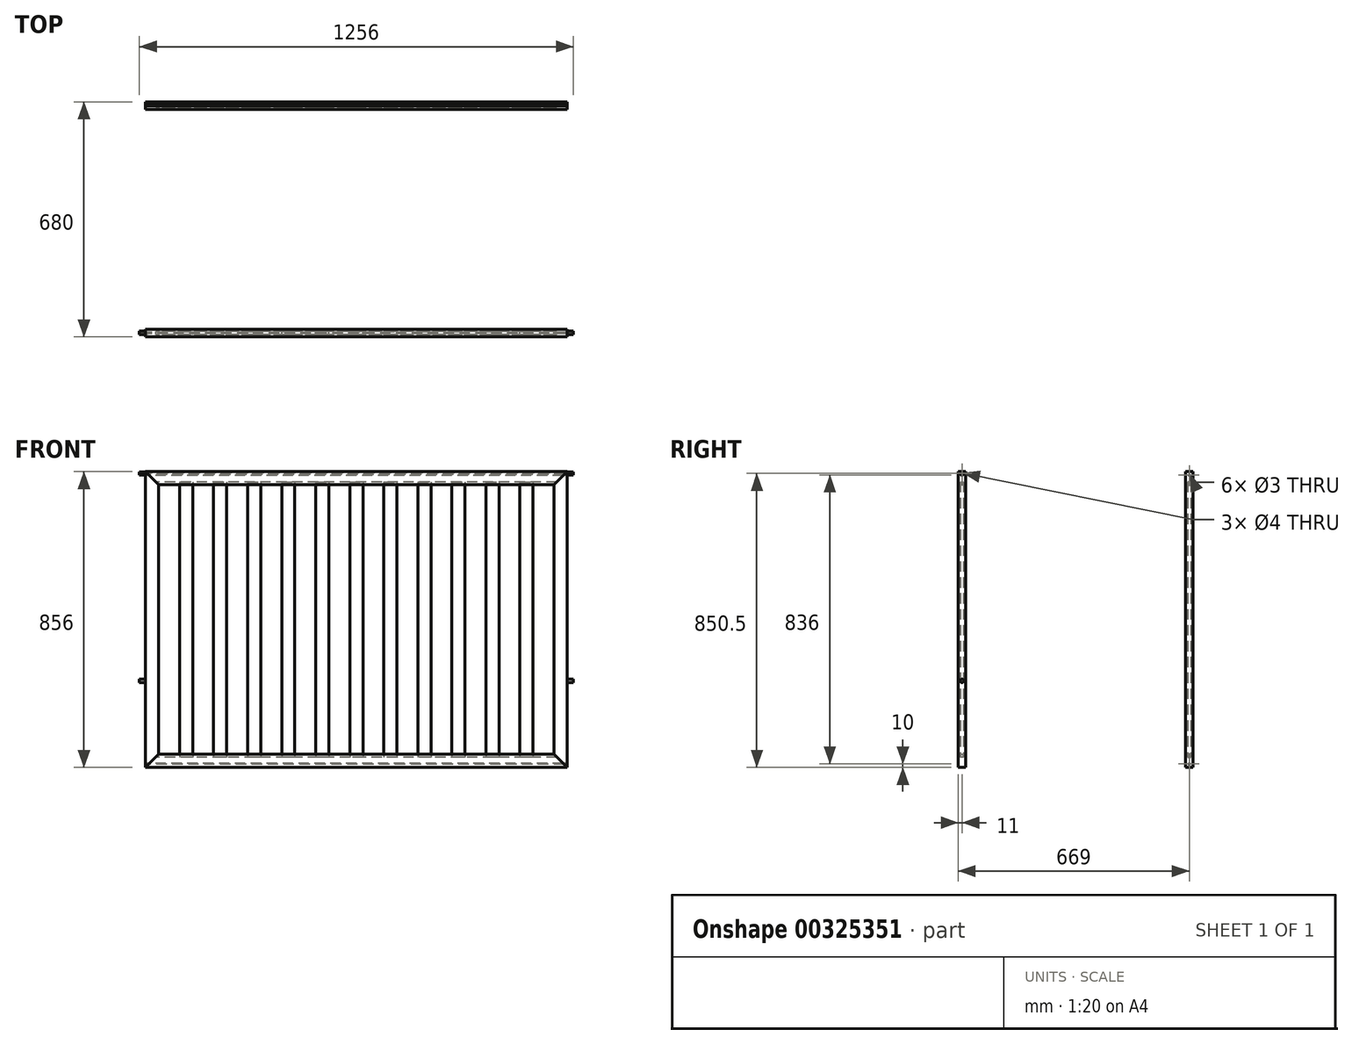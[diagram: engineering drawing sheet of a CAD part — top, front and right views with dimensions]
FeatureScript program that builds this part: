
annotation { "Feature Type Name" : "Feature", "Feature Type Description" : "" }
export const myFeature = defineFeature(function(context is Context, id is Id, definition is map)
    precondition{}
    {
        {
            var Q0;
            Q0=qCreatedBy(makeId("Right.planeOp"),FACE);
            var sketch = newSketch(context, id + "F0", { "sketchPlane" : qUnion([Q0])});
            skLineSegment(sketch, "E0", {"start": v(0, 0) * mm, "end": v(340, 0) * mm, "construction": true});
            skLineSegment(sketch, "E1", {"start": v(340, 0) * mm, "end": v(340, 428) * mm, "construction": true});
            skLineSegment(sketch, "E2.bottom", {"start": v(318, 428) * mm, "end": v(340, 428) * mm});
            skLineSegment(sketch, "E2.top", {"start": v(318, 390) * mm, "end": v(324.5, 390) * mm});
            skLineSegment(sketch, "E2.left", {"start": v(318, 428) * mm, "end": v(318, 390) * mm});
            skLineSegment(sketch, "E2.right", {"start": v(340, 428) * mm, "end": v(340, 390) * mm});
            skLineSegment(sketch, "E3.bottom", {"start": v(333.5, 398) * mm, "end": v(324.5, 398) * mm});
            skLineSegment(sketch, "E3.left", {"start": v(333.5, 398) * mm, "end": v(333.5, 390) * mm});
            skLineSegment(sketch, "E3.right", {"start": v(324.5, 398) * mm, "end": v(324.5, 390) * mm});
            skPoint(sketch, "E3.middle", {"position": v(329, 390) * mm});
            skLineSegment(sketch, "E4.trimOffspring", {"start": v(333.5, 390) * mm, "end": v(340, 390) * mm});
            skLineSegment(sketch, "E5.MirrorCS", {"start": v(318, -390) * mm, "end": v(324.5, -390) * mm});
            skLineSegment(sketch, "E6.MirrorCS", {"start": v(333.5, -390) * mm, "end": v(340, -390) * mm});
            skPoint(sketch, "E7.MirrorP", {"position": v(329, -390) * mm});
            skLineSegment(sketch, "E8.MirrorCS", {"start": v(333.5, -398) * mm, "end": v(333.5, -390) * mm});
            skLineSegment(sketch, "E9.MirrorCS", {"start": v(324.5, -398) * mm, "end": v(324.5, -390) * mm});
            skLineSegment(sketch, "E10.MirrorCS", {"start": v(318, -428) * mm, "end": v(340, -428) * mm});
            skLineSegment(sketch, "E11.MirrorCS", {"start": v(318, -428) * mm, "end": v(318, -390) * mm});
            skLineSegment(sketch, "E12.MirrorCS", {"start": v(333.5, -398) * mm, "end": v(324.5, -398) * mm});
            skLineSegment(sketch, "E13.MirrorCS", {"start": v(340, -428) * mm, "end": v(340, -390) * mm});
            skSolve(sketch);
        }
        {
            var Q0;
            Q0 = qSketchRegion(id + "F0", true);
            extrude(context, id + "F1", {"entities" : qUnion([Q0]), "depth" : 1220 * mm});
        }
        {
            var Q0;
            Q0=makeQuery(id+"F1.opExtrude","SWEPT_FACE",FACE,{"disambiguationData":[OSD([sQuery(id+"F0.wireOp",EDGE,"E2.left")])]});
            var sketch = newSketch(context, id + "F2", { "sketchPlane" : qUnion([Q0])});
            skPoint(sketch, "E14.0", {"position": v(0, 428) * mm});
            skLineSegment(sketch, "E15", {"start": v(0, 0) * mm, "end": v(-300, 0) * mm, "construction": true});
            skPoint(sketch, "E16.MirrorP", {"position": v(0, -428) * mm});
            skLineSegment(sketch, "E17", {"start": v(0, -428) * mm, "end": v(0, 428) * mm});
            skLineSegment(sketch, "E18", {"start": v(38, 390) * mm, "end": v(38, -390) * mm});
            skPoint(sketch, "E19.0", {"position": v(610, 428) * mm});
            skLineSegment(sketch, "E20", {"start": v(610, 428) * mm, "end": v(610, 568) * mm, "construction": true});
            skLineSegment(sketch, "E21", {"start": v(38, 390) * mm, "end": v(0, 428) * mm});
            skLineSegment(sketch, "E22", {"start": v(0, -428) * mm, "end": v(38, -390) * mm});
            skPoint(sketch, "E23.orphan", {"position": v(0, -390) * mm});
            skLineSegment(sketch, "E24.MirrorCS", {"start": v(1182, 390) * mm, "end": v(1220, 428) * mm});
            skLineSegment(sketch, "E25.MirrorCS", {"start": v(1220, -428) * mm, "end": v(1182, -390) * mm});
            skPoint(sketch, "E26.MirrorP", {"position": v(1220, -390) * mm});
            skPoint(sketch, "E27.MirrorP", {"position": v(1220, 428) * mm});
            skLineSegment(sketch, "E28.MirrorCS", {"start": v(1182, 390) * mm, "end": v(1182, -390) * mm});
            skLineSegment(sketch, "E29.MirrorCS", {"start": v(1220, -428) * mm, "end": v(1220, 428) * mm});
            skPoint(sketch, "E30.MirrorP", {"position": v(1220, -428) * mm});
            skSolve(sketch);
        }
        {
            var Q0;
            Q0 = qSketchRegion(id + "F2", true);
            extrude(context, id + "F3", {"entities" : qUnion([Q0]), "operationType" : NewBodyOperationType.REMOVE, "oppositeDirection" : true, "depth" : 350 * mm});
        }
        {
            var Q0;
            Q0 = qSketchRegion(id + "F2", true);
            extrude(context, id + "F4", {"entities" : qUnion([Q0]), "oppositeDirection" : true, "depth" : 22 * mm});
        }
        {
            var Q0;
            Q0=makeQuery(id+"F1.opExtrude","SWEPT_FACE",FACE,{"disambiguationData":[OSD([sQuery(id+"F0.wireOp",EDGE,"E12.MirrorCS")])]});
            var sketch = newSketch(context, id + "F5", { "sketchPlane" : qUnion([Q0])});
            skLineSegment(sketch, "E31.0", {"start": v(98.5, 324.5) * mm, "end": v(38, 324.5) * mm, "construction": true});
            skPoint(sketch, "E32.orphan", {"position": v(38, 324.5) * mm});
            skLineSegment(sketch, "E33.bottom", {"start": v(98.5, 324.5) * mm, "end": v(136.5, 324.5) * mm});
            skLineSegment(sketch, "E33.top", {"start": v(98.5, 333.5) * mm, "end": v(136.5, 333.5) * mm});
            skLineSegment(sketch, "E33.left", {"start": v(98.5, 324.5) * mm, "end": v(98.5, 333.5) * mm});
            skLineSegment(sketch, "E33.right", {"start": v(136.5, 324.5) * mm, "end": v(136.5, 333.5) * mm});
            skLineSegment(sketch, "E34.1.0.0", {"start": v(197, 333.5) * mm, "end": v(235, 333.5) * mm});
            skLineSegment(sketch, "E34.1.0.1", {"start": v(197, 324.5) * mm, "end": v(197, 333.5) * mm});
            skLineSegment(sketch, "E34.1.0.2", {"start": v(197, 324.5) * mm, "end": v(235, 324.5) * mm});
            skLineSegment(sketch, "E34.1.0.3", {"start": v(235, 324.5) * mm, "end": v(235, 333.5) * mm});
            skLineSegment(sketch, "E34.2.0.0", {"start": v(295.5, 333.5) * mm, "end": v(333.5, 333.5) * mm});
            skLineSegment(sketch, "E34.2.0.1", {"start": v(295.5, 324.5) * mm, "end": v(295.5, 333.5) * mm});
            skLineSegment(sketch, "E34.2.0.2", {"start": v(295.5, 324.5) * mm, "end": v(333.5, 324.5) * mm});
            skLineSegment(sketch, "E34.2.0.3", {"start": v(333.5, 324.5) * mm, "end": v(333.5, 333.5) * mm});
            skLineSegment(sketch, "E34.3.0.0", {"start": v(394, 333.5) * mm, "end": v(432, 333.5) * mm});
            skLineSegment(sketch, "E34.3.0.1", {"start": v(394, 324.5) * mm, "end": v(394, 333.5) * mm});
            skLineSegment(sketch, "E34.3.0.2", {"start": v(394, 324.5) * mm, "end": v(432, 324.5) * mm});
            skLineSegment(sketch, "E34.3.0.3", {"start": v(432, 324.5) * mm, "end": v(432, 333.5) * mm});
            skLineSegment(sketch, "E34.4.0.0", {"start": v(492.5, 333.5) * mm, "end": v(530.5, 333.5) * mm});
            skLineSegment(sketch, "E34.4.0.1", {"start": v(492.5, 324.5) * mm, "end": v(492.5, 333.5) * mm});
            skLineSegment(sketch, "E34.4.0.2", {"start": v(492.5, 324.5) * mm, "end": v(530.5, 324.5) * mm});
            skLineSegment(sketch, "E34.4.0.3", {"start": v(530.5, 324.5) * mm, "end": v(530.5, 333.5) * mm});
            skLineSegment(sketch, "E34.5.0.0", {"start": v(591, 333.5) * mm, "end": v(629, 333.5) * mm});
            skLineSegment(sketch, "E34.5.0.1", {"start": v(591, 324.5) * mm, "end": v(591, 333.5) * mm});
            skLineSegment(sketch, "E34.5.0.2", {"start": v(591, 324.5) * mm, "end": v(629, 324.5) * mm});
            skLineSegment(sketch, "E34.5.0.3", {"start": v(629, 324.5) * mm, "end": v(629, 333.5) * mm});
            skLineSegment(sketch, "E34.6.0.0", {"start": v(689.5, 333.5) * mm, "end": v(727.5, 333.5) * mm});
            skLineSegment(sketch, "E34.6.0.1", {"start": v(689.5, 324.5) * mm, "end": v(689.5, 333.5) * mm});
            skLineSegment(sketch, "E34.6.0.2", {"start": v(689.5, 324.5) * mm, "end": v(727.5, 324.5) * mm});
            skLineSegment(sketch, "E34.6.0.3", {"start": v(727.5, 324.5) * mm, "end": v(727.5, 333.5) * mm});
            skLineSegment(sketch, "E34.7.0.0", {"start": v(788, 333.5) * mm, "end": v(826, 333.5) * mm});
            skLineSegment(sketch, "E34.7.0.1", {"start": v(788, 324.5) * mm, "end": v(788, 333.5) * mm});
            skLineSegment(sketch, "E34.7.0.2", {"start": v(788, 324.5) * mm, "end": v(826, 324.5) * mm});
            skLineSegment(sketch, "E34.7.0.3", {"start": v(826, 324.5) * mm, "end": v(826, 333.5) * mm});
            skLineSegment(sketch, "E34.8.0.0", {"start": v(886.5, 333.5) * mm, "end": v(924.5, 333.5) * mm});
            skLineSegment(sketch, "E34.8.0.1", {"start": v(886.5, 324.5) * mm, "end": v(886.5, 333.5) * mm});
            skLineSegment(sketch, "E34.8.0.2", {"start": v(886.5, 324.5) * mm, "end": v(924.5, 324.5) * mm});
            skLineSegment(sketch, "E34.8.0.3", {"start": v(924.5, 324.5) * mm, "end": v(924.5, 333.5) * mm});
            skLineSegment(sketch, "E34.9.0.0", {"start": v(985, 333.5) * mm, "end": v(1023, 333.5) * mm});
            skLineSegment(sketch, "E34.9.0.1", {"start": v(985, 324.5) * mm, "end": v(985, 333.5) * mm});
            skLineSegment(sketch, "E34.9.0.2", {"start": v(985, 324.5) * mm, "end": v(1023, 324.5) * mm});
            skLineSegment(sketch, "E34.9.0.3", {"start": v(1023, 324.5) * mm, "end": v(1023, 333.5) * mm});
            skLineSegment(sketch, "E34.10.0.0", {"start": v(1083.5, 333.5) * mm, "end": v(1121.5, 333.5) * mm});
            skLineSegment(sketch, "E34.10.0.1", {"start": v(1083.5, 324.5) * mm, "end": v(1083.5, 333.5) * mm});
            skLineSegment(sketch, "E34.10.0.2", {"start": v(1083.5, 324.5) * mm, "end": v(1121.5, 324.5) * mm});
            skLineSegment(sketch, "E34.10.0.3", {"start": v(1121.5, 324.5) * mm, "end": v(1121.5, 333.5) * mm});
            skLineSegment(sketch, "E34.direction1", {"start": v(98.5, 324.5) * mm, "end": v(197, 324.5) * mm, "construction": true});
            skSolve(sketch);
        }
        {
            var Q0;
            Q0 = qSketchRegion(id + "F5", true);
            var Q1;
            Q1=makeQuery(id+"F1.opExtrude","SWEPT_FACE",FACE,{"disambiguationData":[OSD([sQuery(id+"F0.wireOp",EDGE,"E3.bottom")])]});
            extrude(context, id + "F6", {"entities" : qUnion([Q0]), "endBound" : BoundingType.UP_TO_SURFACE, "endBoundEntityFace" : qUnion([Q1]), "depth" : 25 * mm});
        }
        {
            var Q0;
            Q0=qCreatedBy(makeId("Right.planeOp"),FACE);
            var sketch = newSketch(context, id + "F7", { "sketchPlane" : qUnion([Q0])});
            skLineSegment(sketch, "E35.bottom", {"start": v(318, 435) * mm, "end": v(340, 435) * mm, "construction": true});
            skLineSegment(sketch, "E35.top", {"start": v(318, 400) * mm, "end": v(340, 400) * mm, "construction": true});
            skLineSegment(sketch, "E35.left", {"start": v(318, 435) * mm, "end": v(318, 400) * mm, "construction": true});
            skLineSegment(sketch, "E35.right", {"start": v(340, 435) * mm, "end": v(340, 400) * mm, "construction": true});
            skLineSegment(sketch, "E36", {"start": v(329, 435) * mm, "end": v(329, 429) * mm, "construction": true});
            skLineSegment(sketch, "E37", {"start": v(329, 429) * mm, "end": v(329, 418) * mm, "construction": true});
            skCircle(sketch, "E38", {"center": v(329, 429) * mm, "radius": 2.5 * mm});
            skCircle(sketch, "E39", {"center": v(329, 418) * mm, "radius": 2.5 * mm});
            skLineSegment(sketch, "E40", {"start": v(0, 0) * mm, "end": v(-140, 0) * mm, "construction": true});
            skLineSegment(sketch, "E41.MirrorCS", {"start": v(318, -435) * mm, "end": v(340, -435) * mm, "construction": true});
            skLineSegment(sketch, "E42.MirrorCS", {"start": v(340, -435) * mm, "end": v(340, -400) * mm, "construction": true});
            skLineSegment(sketch, "E43.MirrorCS", {"start": v(318, -435) * mm, "end": v(318, -400) * mm, "construction": true});
            skLineSegment(sketch, "E44.MirrorCS", {"start": v(318, -400) * mm, "end": v(340, -400) * mm, "construction": true});
            skCircle(sketch, "E45.MirrorC", {"center": v(329, -418) * mm, "radius": 2.5 * mm});
            skCircle(sketch, "E46.MirrorC", {"center": v(329, -429) * mm, "radius": 2.5 * mm});
            skLineSegment(sketch, "E47", {"start": v(0, 0) * mm, "end": v(0, 200) * mm, "construction": true});
            skLineSegment(sketch, "E48.MirrorCS", {"start": v(-318, -435) * mm, "end": v(-318, -400) * mm, "construction": true});
            skLineSegment(sketch, "E49.MirrorCS", {"start": v(-318, -400) * mm, "end": v(-340, -400) * mm, "construction": true});
            skLineSegment(sketch, "E50.MirrorCS", {"start": v(-340, -435) * mm, "end": v(-340, -400) * mm, "construction": true});
            skLineSegment(sketch, "E51.MirrorCS", {"start": v(-318, -435) * mm, "end": v(-340, -435) * mm, "construction": true});
            skLineSegment(sketch, "E52.MirrorCS", {"start": v(-318, 400) * mm, "end": v(-340, 400) * mm, "construction": true});
            skLineSegment(sketch, "E53.MirrorCS", {"start": v(-318, 435) * mm, "end": v(-318, 400) * mm, "construction": true});
            skLineSegment(sketch, "E54.MirrorCS", {"start": v(-340, 435) * mm, "end": v(-340, 400) * mm, "construction": true});
            skLineSegment(sketch, "E55.MirrorCS", {"start": v(-318, 435) * mm, "end": v(-340, 435) * mm, "construction": true});
            skLineSegment(sketch, "E56", {"start": v(-329, 435) * mm, "end": v(-329, 422.5) * mm, "construction": true});
            skPoint(sketch, "E56.endSnap0", {"position": v(-329, 435) * mm});
            skArc(sketch, "E57", {"start": v(-323.5, 422.5) * mm, "mid": v(-329, 428) * mm, "end": v(-334.5, 422.5) * mm});
            skArc(sketch, "E58.0.1.0", {"start": v(-334.5, 282.5) * mm, "mid": v(-329, 277) * mm, "end": v(-323.5, 282.5) * mm});
            skLineSegment(sketch, "E58.direction2", {"start": v(-329, 422.5) * mm, "end": v(-329, 282.5) * mm, "construction": true});
            skLineSegment(sketch, "E59.0", {"start": v(-334.5, 422.5) * mm, "end": v(-334.5, 282.5) * mm});
            skLineSegment(sketch, "E60.0.1.0", {"start": v(-334.5, -177.5) * mm, "end": v(-334.5, -317.5) * mm});
            skArc(sketch, "E60.0.1.2", {"start": v(-323.5, -177.5) * mm, "mid": v(-329, -172) * mm, "end": v(-334.5, -177.5) * mm});
            skArc(sketch, "E60.0.1.3", {"start": v(-334.5, -317.5) * mm, "mid": v(-329, -323) * mm, "end": v(-323.5, -317.5) * mm});
            skLineSegment(sketch, "E60.direction1", {"start": v(-334.5, 282.5) * mm, "end": v(-313.5, 282.5) * mm, "construction": true});
            skLineSegment(sketch, "E60.direction2", {"start": v(-334.5, 282.5) * mm, "end": v(-334.5, -317.5) * mm, "construction": true});
            skLineSegment(sketch, "E61", {"start": v(-323.5, -317.5) * mm, "end": v(-323.5, -177.5) * mm});
            skSolve(sketch);
        }
        {
            var Q0;
            Q0=makeQuery(id+"F4.opExtrude","SWEPT_BODY",BODY,{"disambiguationData":[OSD([sQuery(id+"F2.wireOp",EDGE,"b1047d30-6eb7-4597-bc75-de0ae35a6d8d0.MirrorCS"),sQuery(id+"F2.wireOp",EDGE,"b1047d30-6eb7-4597-bc75-de0ae35a6d8d1.MirrorCS"),sQuery(id+"F2.wireOp",EDGE,"b1047d30-6eb7-4597-bc75-de0ae35a6d8d3.MirrorCS"),sQuery(id+"F2.wireOp",EDGE,"b1047d30-6eb7-4597-bc75-de0ae35a6d8d4.MirrorCS")])]});
            var Q1;
            Q1=makeQuery(id+"F6.opExtrude","SWEPT_BODY",BODY,{"disambiguationData":[OSD([sQuery(id+"F5.wireOp",EDGE,"E34.6.0.0"),sQuery(id+"F5.wireOp",EDGE,"E34.6.0.1"),sQuery(id+"F5.wireOp",EDGE,"E34.6.0.2"),sQuery(id+"F5.wireOp",EDGE,"E34.6.0.3")])]});
            var Q2;
            Q2=makeQuery(id+"F6.opExtrude","SWEPT_BODY",BODY,{"disambiguationData":[OSD([sQuery(id+"F5.wireOp",EDGE,"E34.11.0.0"),sQuery(id+"F5.wireOp",EDGE,"E34.11.0.1"),sQuery(id+"F5.wireOp",EDGE,"E34.11.0.2"),sQuery(id+"F5.wireOp",EDGE,"E34.11.0.3")])]});
            var Q3;
            Q3=makeQuery(id+"F6.opExtrude","SWEPT_BODY",BODY,{"disambiguationData":[OSD([sQuery(id+"F5.wireOp",EDGE,"E34.5.0.0"),sQuery(id+"F5.wireOp",EDGE,"E34.5.0.1"),sQuery(id+"F5.wireOp",EDGE,"E34.5.0.2"),sQuery(id+"F5.wireOp",EDGE,"E34.5.0.3")])]});
            var Q4;
            Q4=makeQuery(id+"F6.opExtrude","SWEPT_BODY",BODY,{"disambiguationData":[OSD([sQuery(id+"F5.wireOp",EDGE,"E34.7.0.0"),sQuery(id+"F5.wireOp",EDGE,"E34.7.0.1"),sQuery(id+"F5.wireOp",EDGE,"E34.7.0.2"),sQuery(id+"F5.wireOp",EDGE,"E34.7.0.3")])]});
            var Q5;
            Q5=makeQuery(id+"F6.opExtrude","SWEPT_BODY",BODY,{"disambiguationData":[OSD([sQuery(id+"F5.wireOp",EDGE,"E34.10.0.0"),sQuery(id+"F5.wireOp",EDGE,"E34.10.0.1"),sQuery(id+"F5.wireOp",EDGE,"E34.10.0.2"),sQuery(id+"F5.wireOp",EDGE,"E34.10.0.3")])]});
            var Q6;
            Q6=makeQuery(id+"F6.opExtrude","SWEPT_BODY",BODY,{"disambiguationData":[OSD([sQuery(id+"F5.wireOp",EDGE,"E34.4.0.0"),sQuery(id+"F5.wireOp",EDGE,"E34.4.0.1"),sQuery(id+"F5.wireOp",EDGE,"E34.4.0.2"),sQuery(id+"F5.wireOp",EDGE,"E34.4.0.3")])]});
            var Q7;
            Q7=makeQuery(id+"F6.opExtrude","SWEPT_BODY",BODY,{"disambiguationData":[OSD([sQuery(id+"F5.wireOp",EDGE,"E34.9.0.0"),sQuery(id+"F5.wireOp",EDGE,"E34.9.0.1"),sQuery(id+"F5.wireOp",EDGE,"E34.9.0.2"),sQuery(id+"F5.wireOp",EDGE,"E34.9.0.3")])]});
            var Q8;
            Q8=makeQuery(id+"F6.opExtrude","SWEPT_BODY",BODY,{"disambiguationData":[OSD([sQuery(id+"F5.wireOp",EDGE,"E34.3.0.0"),sQuery(id+"F5.wireOp",EDGE,"E34.3.0.1"),sQuery(id+"F5.wireOp",EDGE,"E34.3.0.2"),sQuery(id+"F5.wireOp",EDGE,"E34.3.0.3")])]});
            var Q9;
            Q9=makeQuery(id+"F6.opExtrude","SWEPT_BODY",BODY,{"disambiguationData":[OSD([sQuery(id+"F5.wireOp",EDGE,"E34.2.0.0"),sQuery(id+"F5.wireOp",EDGE,"E34.2.0.1"),sQuery(id+"F5.wireOp",EDGE,"E34.2.0.2"),sQuery(id+"F5.wireOp",EDGE,"E34.2.0.3")])]});
            var Q10;
            Q10=makeQuery(id+"F6.opExtrude","SWEPT_BODY",BODY,{"disambiguationData":[OSD([sQuery(id+"F5.wireOp",EDGE,"E33.bottom"),sQuery(id+"F5.wireOp",EDGE,"E33.top"),sQuery(id+"F5.wireOp",EDGE,"E33.left"),sQuery(id+"F5.wireOp",EDGE,"E33.right")])]});
            var Q11;
            Q11=makeQuery(id+"F6.opExtrude","SWEPT_BODY",BODY,{"disambiguationData":[OSD([sQuery(id+"F5.wireOp",EDGE,"E34.1.0.0"),sQuery(id+"F5.wireOp",EDGE,"E34.1.0.1"),sQuery(id+"F5.wireOp",EDGE,"E34.1.0.2"),sQuery(id+"F5.wireOp",EDGE,"E34.1.0.3")])]});
            var Q12;
            Q12=makeQuery(id+"F1.opExtrude","SWEPT_BODY",BODY,{"disambiguationData":[OSD([sQuery(id+"F0.wireOp",EDGE,"E2.bottom"),sQuery(id+"F0.wireOp",EDGE,"E2.top"),sQuery(id+"F0.wireOp",EDGE,"E2.left"),sQuery(id+"F0.wireOp",EDGE,"E2.right"),sQuery(id+"F0.wireOp",EDGE,"E3.bottom"),sQuery(id+"F0.wireOp",EDGE,"E3.left"),sQuery(id+"F0.wireOp",EDGE,"E3.right"),sQuery(id+"F0.wireOp",EDGE,"E4.trimOffspring")])]});
            var Q13;
            Q13=makeQuery(id+"F6.opExtrude","SWEPT_BODY",BODY,{"disambiguationData":[OSD([sQuery(id+"F5.wireOp",EDGE,"E34.8.0.0"),sQuery(id+"F5.wireOp",EDGE,"E34.8.0.1"),sQuery(id+"F5.wireOp",EDGE,"E34.8.0.2"),sQuery(id+"F5.wireOp",EDGE,"E34.8.0.3")])]});
            var Q14;
            Q14=makeQuery(id+"F4.opExtrude","SWEPT_BODY",BODY,{"disambiguationData":[OSD([sQuery(id+"F2.wireOp",EDGE,"6JQJvKk6-9tsE-XuLx-Z2kx-k19th0KeuHWZ"),sQuery(id+"F2.wireOp",EDGE,"8ad1f134-3218-4958-96c1-cced4667ce510.MirrorCS"),sQuery(id+"F2.wireOp",EDGE,"E17"),sQuery(id+"F2.wireOp",EDGE,"E18")])]});
            var Q15;
            Q15=makeQuery(id+"F1.opExtrude","SWEPT_BODY",BODY,{"disambiguationData":[OSD([sQuery(id+"F0.wireOp",EDGE,"E5.MirrorCS"),sQuery(id+"F0.wireOp",EDGE,"E6.MirrorCS"),sQuery(id+"F0.wireOp",EDGE,"E8.MirrorCS"),sQuery(id+"F0.wireOp",EDGE,"E9.MirrorCS"),sQuery(id+"F0.wireOp",EDGE,"E10.MirrorCS"),sQuery(id+"F0.wireOp",EDGE,"E11.MirrorCS"),sQuery(id+"F0.wireOp",EDGE,"E12.MirrorCS"),sQuery(id+"F0.wireOp",EDGE,"E13.MirrorCS")])]});
            var Q16;
            Q16=makeQuery(id+"F4.opExtrude","SWEPT_BODY",BODY,{"disambiguationData":[OSD([sQuery(id+"F2.wireOp",EDGE,"E24.MirrorCS"),sQuery(id+"F2.wireOp",EDGE,"E25.MirrorCS"),sQuery(id+"F2.wireOp",EDGE,"E28.MirrorCS"),sQuery(id+"F2.wireOp",EDGE,"E29.MirrorCS")])]});
            var Q17;
            Q17=qCreatedBy(makeId("Front.planeOp"),FACE);
            mirror(context, id + "F8", {"entities" : qUnion([Q0, Q1, Q2, Q3, Q4, Q5, Q6, Q7, Q8, Q9, Q10, Q11, Q12, Q13, Q14, Q15, Q16]), "mirrorPlane" : qUnion([Q17])});
        }
        {
            var Q0;
            Q0=makeQuery(id+"F4.opExtrude","SWEPT_FACE",FACE,{"disambiguationData":[OSD([sQuery(id+"F2.wireOp",EDGE,"E17")])]});
            var sketch = newSketch(context, id + "F9", { "sketchPlane" : qUnion([Q0])});
            skPoint(sketch, "E62.0", {"position": v(-329, -418) * mm});
            skPoint(sketch, "E62.1", {"position": v(-329, -429) * mm});
            skPoint(sketch, "E62.2", {"position": v(-329, 429) * mm});
            skPoint(sketch, "E62.3", {"position": v(-329, 418) * mm});
            skCircle(sketch, "E63", {"center": v(-329, 429) * mm, "radius": 1.5 * mm});
            skCircle(sketch, "E64", {"center": v(-329, 418) * mm, "radius": 1.5 * mm});
            skCircle(sketch, "E65", {"center": v(-329, -418) * mm, "radius": 1.5 * mm});
            skCircle(sketch, "E66", {"center": v(-329, -429) * mm, "radius": 1.5 * mm});
            skSolve(sketch);
        }
        {
            var Q0;
            Q0 = qSketchRegion(id + "F9", true);
            var Q1;
            Q1 = qConstructionFilter(qBodyType(qCreatedBy(id + "F9" ,EDGE), BodyType.WIRE), ConstructionObject.NO);
            extrude(context, id + "F10", {"entities" : qUnion([Q0]), "operationType" : NewBodyOperationType.REMOVE, "surfaceEntities" : qUnion([Q1]), "endBound" : BoundingType.THROUGH_ALL, "oppositeDirection" : true, "depth" : 50 * mm});
        }
        {
            var Q0;
            Q0=makeQuery(id+"F8.opPattern","COPY",FACE,{"derivedFrom":makeQuery(id+"F4.opExtrude","SWEPT_FACE",FACE,{"disambiguationData":[OSD([sQuery(id+"F2.wireOp",EDGE,"E17")])]}),"instanceName":"1"});
            var sketch = newSketch(context, id + "F11", { "sketchPlane" : qUnion([Q0])});
            skPoint(sketch, "E67.0", {"position": v(329, 422.5) * mm});
            skPoint(sketch, "E68.0", {"position": v(329, -177.5) * mm});
            skCircle(sketch, "E69", {"center": v(329, 422.5) * mm, "radius": 5 * mm});
            skCircle(sketch, "E70", {"center": v(329, -177.5) * mm, "radius": 5 * mm});
            skSolve(sketch);
        }
        {
            var Q0;
            Q0 = qSketchRegion(id + "F11", true);
            extrude(context, id + "F12", {"entities" : qUnion([Q0]), "depth" : 18 * mm});
        }
        {
            var Q0;
            Q0=makeQuery(id+"F8.opPattern","COPY",EDGE,{"derivedFrom":makeQuery(id+"F1.opExtrude","SWEPT_EDGE",EDGE,{"disambiguationData":[OSD([sQuery(id+"F0.wireOp",EDGE,"E2.bottom"),sQuery(id+"F0.wireOp",EDGE,"E2.right")])]}),"instanceName":"1"});
            cPoint(context, id + "F13", {"entities" : qUnion([Q0]), "parameter" : 0.5});
        }
        {
            var Q0;
            Q0=makeQuery(id+"F8.opPattern","COPY",FACE,{"derivedFrom":makeQuery(id+"F4.opExtrude","SWEPT_FACE",FACE,{"disambiguationData":[OSD([sQuery(id+"F2.wireOp",EDGE,"E17")])]}),"instanceName":"1"});
            var Q1;
            Q1 = qCreatedBy(id + "F13" ,VERTEX);
            cPlane(context, id + "F14", {"entities" : qUnion([Q0, Q1]), "cplaneType" : CPlaneType.PLANE_POINT, "offset" : 25 * mm, "width" : 150 * mm, "height" : 150 * mm});
        }
        {
            var Q0;
            Q0=makeQuery(id+"F12.opExtrude","SWEPT_BODY",BODY,{"disambiguationData":[OSD([sQuery(id+"F11.wireOp",EDGE,"E69")])]});
            var Q1;
            Q1=makeQuery(id+"F12.opExtrude","SWEPT_BODY",BODY,{"disambiguationData":[OSD([sQuery(id+"F11.wireOp",EDGE,"E70")])]});
            var Q2;
            Q2=qCreatedBy(id+"F14.planeOp",FACE);
            mirror(context, id + "F15", {"operationType" : NewBodyOperationType.ADD, "entities" : qUnion([Q0, Q1]), "mirrorPlane" : qUnion([Q2])});
        }
        {
            var Q0;
            Q0=makeQuery(id+"F12.opExtrude","CAP_FACE",FACE,{"disambiguationData":[OSD([sQuery(id+"F11.wireOp",EDGE,"E69")])],"isStart":false});
            var sketch = newSketch(context, id + "F16", { "sketchPlane" : qUnion([Q0])});
            skCircle(sketch, "E71", {"center": v(329, 422.5) * mm, "radius": 2 * mm});
            skSolve(sketch);
        }
        {
            var Q0;
            Q0 = qSketchRegion(id + "F16", true);
            var Q1;
            Q1=makeQuery(id+"F15.opPattern","COPY",FACE,{"derivedFrom":makeQuery(id+"F12.opExtrude","CAP_FACE",FACE,{"disambiguationData":[OSD([sQuery(id+"F11.wireOp",EDGE,"E69")])],"isStart":false}),"instanceName":"1"});
            extrude(context, id + "F17", {"entities" : qUnion([Q0]), "operationType" : NewBodyOperationType.REMOVE, "endBound" : BoundingType.UP_TO_SURFACE, "oppositeDirection" : true, "endBoundEntityFace" : qUnion([Q1]), "depth" : 1256 * mm});
        }
    });
